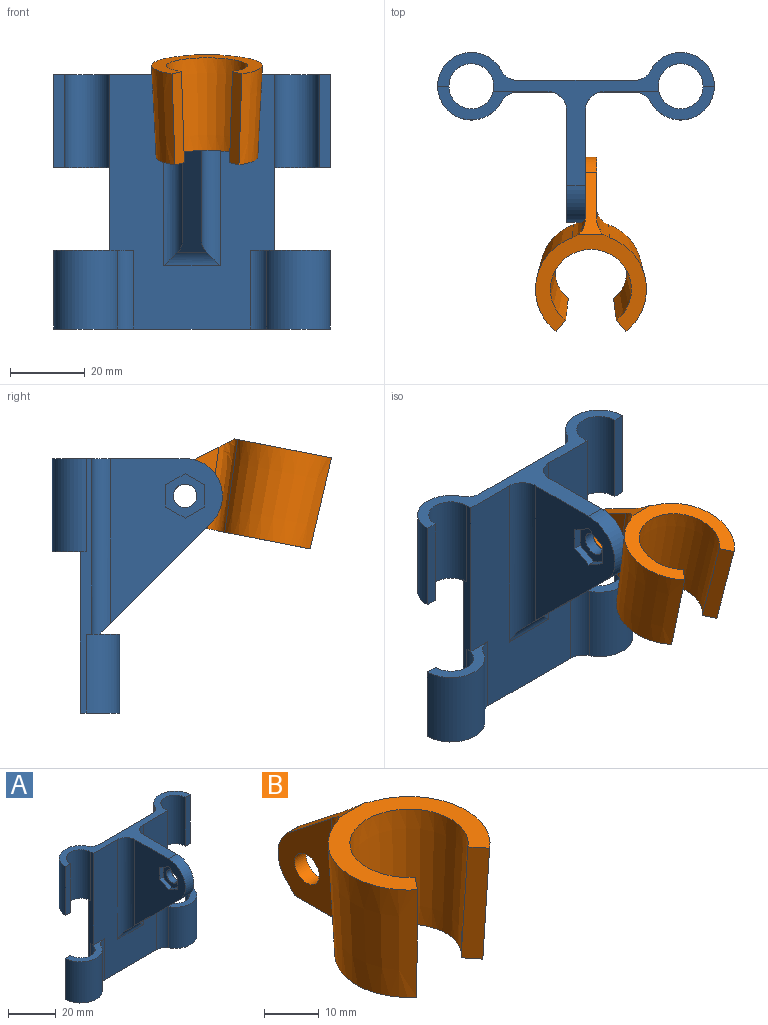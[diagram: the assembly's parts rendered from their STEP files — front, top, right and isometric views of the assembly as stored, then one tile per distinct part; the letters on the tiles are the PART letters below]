
ASSEMBLY  parts=2 mates=1
PART A: 41 faces, bbox 74x45.5x68.1 mm
  f0: plane 44.14x30mm, normal (-1,0,0), area 758.8mm2, adj f22,f24,f26,f27,f28,f29,f30,f31
  f1: cylinder r=3.15mm len=6.3mm, axis (-1,0,0), area 59.4mm2, adj f25,f33
  f2: plane 21.4x9mm, normal (0,0,1), area 68.2mm2, adj f3,f4,f10,f11,f12,f39
  f3: cylinder r=9mm len=21.1mm, axis (0,0,-1), area 504.9mm2, adj f2,f12,f14,f39
  f4: plane 68.1x44mm, normal (0,-1,0), area 1958.1mm2, adj f2,f8,f10,f13,f14,f22,f34,f35
  f5: cylinder r=9mm len=21.1mm, axis (0,0,-1), area 504.9mm2, adj f6,f13,f14,f40
  f6: plane 21.1x3mm, normal (0,1,0), area 63.3mm2, adj f5,f7,f13,f14
  f7: cylinder r=6mm len=21.1mm, axis (0,0,-1), area 397.7mm2, adj f6,f8,f13,f14
  f8: plane 68.1x3mm, normal (1,0,0), area 135.2mm2, adj f4,f7,f9,f13,f14,f17,f22,f23
  f9: plane 68.1x44mm, normal (0,1,0), area 2676.4mm2, adj f8,f10,f14,f15,f22,f23,f37,f38
  f10: plane 68.1x3mm, normal (-1,0,0), area 135.1mm2, adj f2,f4,f9,f11,f14,f15,f16,f22
  f11: cylinder r=6mm len=21.1mm, axis (0,0,-1), area 397.7mm2, adj f2,f10,f12,f14
  f12: plane 21.1x3mm, normal (0,1,0), area 63.3mm2, adj f2,f3,f11,f14
  f13: plane 21.4x9mm, normal (0,0,1), area 68.2mm2, adj f4,f5,f6,f7,f8,f40
  f14: plane 74x10.5mm, normal (0,0,-1), area 268.5mm2, adj f3,f4,f5,f6,f7,f8,f9,f10
  f15: plane 21.4x9mm, normal (0,0,-1), area 68.2mm2, adj f9,f10,f16,f20,f21,f37
  f16: cylinder r=6mm len=25mm, axis (0,0,-1), area 471.2mm2, adj f10,f15,f21,f22
  f17: cylinder r=6mm len=25mm, axis (0,0,-1), area 471.2mm2, adj f8,f18,f22,f23
  f18: plane 25x3mm, normal (0,-1,0), area 75mm2, adj f17,f19,f22,f23
  f19: cylinder r=9mm len=25mm, axis (0,0,-1), area 598.2mm2, adj f18,f22,f23,f38
  f20: cylinder r=9mm len=25mm, axis (0,0,-1), area 598.2mm2, adj f15,f21,f22,f37
  f21: plane 25x3mm, normal (0,-1,0), area 75mm2, adj f15,f16,f20,f22
  f22: plane 74x35.5mm, normal (0,0,1), area 404.2mm2, adj f0,f4,f8,f9,f10,f16,f17,f18
  f23: plane 21.4x9mm, normal (0,0,-1), area 68.2mm2, adj f8,f9,f17,f18,f19,f38
  f24: plane 30.61x30.61mm, normal (0,-0.71,-0.71), area 221mm2, adj f0,f25,f26,f34,f35,f36
  f25: plane 44.14x30mm, normal (1,0,0), area 819.5mm2, adj f1,f22,f24,f26,f34
  f26: cylinder r=10mm len=17.07mm, axis (-1,0,0), area 117.8mm2, adj f0,f22,f24,f25
  f27: plane 5.15x2.97mm, normal (0,0.5,-0.87), area 11.9mm2, adj f0,f28,f32,f33
  f28: plane 5.15x2.97mm, normal (0,-0.5,-0.87), area 11.9mm2, adj f0,f27,f29,f33
  f29: plane 5.95x2mm, normal (0,-1,0), area 11.9mm2, adj f0,f28,f30,f33
  f30: plane 5.15x2.97mm, normal (0,-0.5,0.87), area 11.9mm2, adj f0,f29,f31,f33
  f31: plane 5.15x2.97mm, normal (0,0.5,0.87), area 11.9mm2, adj f0,f30,f32,f33
  f32: plane 5.95x2mm, normal (0,1,0), area 11.9mm2, adj f0,f27,f31,f33
  f33: plane 11.89x10.3mm, normal (-1,0,0), area 60.7mm2, adj f1,f27,f28,f29,f30,f31,f32
  f34: cylinder r=5mm len=51.21mm, axis (0,0,-1), area 374.5mm2, adj f4,f22,f24,f25,f36
  f35: cylinder r=5mm len=51.21mm, axis (0,0,1), area 374.5mm2, adj f0,f4,f22,f24,f36
  f36: cylinder r=5mm len=15mm, axis (-1,0,0), area 44.3mm2, adj f4,f24,f34,f35
  f37: cylinder r=5mm len=25mm, axis (0,0,-1), area 136mm2, adj f9,f15,f20,f22
  f38: cylinder r=5mm len=25mm, axis (0,0,-1), area 136mm2, adj f9,f19,f22,f23
  f39: cylinder r=5mm len=21.1mm, axis (0,0,-1), area 114.8mm2, adj f2,f3,f4,f14
  f40: cylinder r=5mm len=21.1mm, axis (0,0,-1), area 114.8mm2, adj f4,f5,f13,f14
PART B: 15 faces, bbox 30x44.3x49.3 mm
  f0: cone r=13.6mm half-angle=2.9deg, axis (0,0,1), area 753.6mm2, adj f1,f3,f5,f14
  f1: plane 38.77x27.3mm, normal (0,0,-1), area 277.6mm2, adj f0,f2,f4,f5,f6,f7,f11,f12
  f2: cone r=13.6mm half-angle=2.9deg, axis (0,0,1), area 753.6mm2, adj f1,f3,f6,f13
  f3: plane 29.75x26.43mm, normal (0,0,1), area 254.6mm2, adj f0,f2,f4,f5,f6,f10,f13,f14
  f4: cone r=10.85mm half-angle=2.9deg, axis (0,0,1), area 1259.7mm2, adj f1,f3,f5,f6
  f5: plane 25x4.08mm, normal (0.78,-0.63,0), area 100.1mm2, adj f0,f1,f3,f4
  f6: plane 25x4.08mm, normal (-0.78,-0.63,0), area 100.1mm2, adj f1,f2,f3,f4
  f7: plane 3x2.2mm, normal (0,0.71,-0.71), area 9.3mm2, adj f1,f8,f11,f12
  f8: cylinder r=7.5mm len=11.2mm, axis (-1,0,0), area 38mm2, adj f7,f10,f11,f12
  f9: cylinder r=3.2mm len=6.4mm, axis (-1,0,0), area 60.3mm2, adj f11,f12
  f10: plane 15.02x11.84mm, normal (0,0.62,0.79), area 61.8mm2, adj f3,f8,f11,f12,f13,f14
  f11: plane 22.05x15.06mm, normal (1,0,0), area 198.5mm2, adj f1,f7,f8,f9,f10,f13
  f12: plane 22.05x15.06mm, normal (-1,0,0), area 198.5mm2, adj f1,f7,f8,f9,f10,f14
  f13: bspline ~49.01x7.25mm, area 146.9mm2, adj f1,f2,f3,f10,f11
  f14: bspline ~49.01x7.25mm, area 146.9mm2, adj f0,f1,f3,f10,f12
PLACE A t=(9.3,-0.51,-28.84)mm fixed
PLACE B rot(axis=(1,0,0),11deg) t=(13.3,-50.11,17.12)mm
MATE revolute B.f8 <-> A.f1  axis (-1,0,0) through (11.8,-27.01,29.26)mm
